# Revit family: Rohrschlaufe SLH
name_source: partatom
category: HLS-Bauteile
revit_build: Autodesk Revit 2017 (Build: 20190507_1515(x64)
units: mm (PartAtom-declared; Revit-internal decimal feet)

## family parameters
Arbeitsebenenbasiert = Ja
Beim Laden mit Abzugskörper schneiden = Nein
Bemaßung runder Anschluss = Durchmesser verwenden
Gemeinsam genutzt = Ja
Immer vertikal = Nein
Raumberechnungspunkt = Nein
Teiletyp = Normal

## types (14) — shared parameters
Fabrikat = Jiangmen Eurofix
Firma = MEFA Befestigungs- und Montagesysteme GmbH
Kurztext1 = Rohrschlaufe SLH
Material = Stahl
Materialname = DX51D
Mengeneinheit = St
Oberflaeche = feuerbandverzinkt
Vorgabe-Ansicht = 1219 mm

## per-type parameters (varying)
| type | Anschluss | Artikelnummer | C | D | EAN | Flanschenmutter | Gewicht | Gewicht pro Bauteil | H | H1 | H2 | Höhe zur Rohrachse | Kurztext2 | MB | MD | Rohraußendurchmesser | Rohraußendurchmesser Zoll | Schlaufentopf | d1 | max. zul. Last | vpe |
| Rohrschlaufe SLH, M10, Ø 33,7 | M10 | 47072034 | 17 mm  [stored 0.0557743 ft] | 34 mm | 4250928450234 | 6kt-Mutter parametrik : Flanschmutter M10 | 0.08 kg | 0.08 kg | 55 mm  [stored 0.180446 ft] | 8 mm  [stored 0.0262467 ft] | 18 mm  [stored 0.0590551 ft] | 63 mm | 1 Zoll / 33,7 mm M10 | 10 mm  [stored 0.0328084 ft] | 2 mm  [stored 0.00656168 ft] | 34 mm | 1 Zoll | Schlaufentopf : Schlaufentopf M10 | 25 mm  [stored 0.082021 ft] | 2.00 kN | 100 St |
| Rohrschlaufe SLH, M10, Ø 42,4 | M10 | 47072042 | 17 mm  [stored 0.0557743 ft] | 42 mm | 4250928450241 | 6kt-Mutter parametrik : Flanschmutter M10 | 0.08 kg | 0.08 kg | 55 mm  [stored 0.180446 ft] | 8 mm  [stored 0.0262467 ft] | 18 mm  [stored 0.0590551 ft] | 68 mm | 1 1/4 Zoll / 42,2 mm M10 | 10 mm  [stored 0.0328084 ft] | 2 mm  [stored 0.00656168 ft] | 42 mm | 1 1/4 Zoll | Schlaufentopf : Schlaufentopf M10 | 25 mm  [stored 0.082021 ft] | 2.00 kN | 100 St |
| Rohrschlaufe SLH, M10, Ø 48,3 | M10 | 47072048 | 17 mm  [stored 0.0557743 ft] | 48 mm | 4250928450258 | 6kt-Mutter parametrik : Flanschmutter M10 | 0.08 kg | 0.08 kg | 60 mm  [stored 0.19685 ft] | 8 mm  [stored 0.0262467 ft] | 18 mm  [stored 0.0590551 ft] | 73 mm | 1 1/2 Zoll / 48,3 mm M10 | 10 mm  [stored 0.0328084 ft] | 2 mm  [stored 0.00656168 ft] | 48 mm | 1 1/2 Zoll | Schlaufentopf : Schlaufentopf M10 | 25 mm  [stored 0.082021 ft] | 2.00 kN | 50 St |
| Rohrschlaufe SLH, M10, Ø 60,3 | M10 | 47072060 | 17 mm  [stored 0.0557743 ft] | 60 mm  [stored 0.19685 ft] | 4250928450265 | 6kt-Mutter parametrik : Flanschmutter M10 | 0.09 kg | 0.09 kg | 69 mm  [stored 0.226378 ft] | 8 mm  [stored 0.0262467 ft] | 18 mm  [stored 0.0590551 ft] | 82 mm | 2 Zoll / 60,3 mm M10 | 10 mm  [stored 0.0328084 ft] | 2 mm  [stored 0.00656168 ft] | 60 mm  [stored 0.19685 ft] | 2 Zoll | Schlaufentopf : Schlaufentopf M10 | 25 mm  [stored 0.082021 ft] | 2.00 kN | 50 St |
| Rohrschlaufe SLH, M10, Ø 76,1 | M10 | 47072076 | 17 mm  [stored 0.0557743 ft] | 76 mm | 4250928450272 | 6kt-Mutter parametrik : Flanschmutter M10 | 0.15 kg | 0.15 kg | 85 mm  [stored 0.278871 ft] | 8 mm  [stored 0.0262467 ft] | 18 mm  [stored 0.0590551 ft] | 99 mm | 2 1/2 Zoll / 76,1 mm M10 | 10 mm  [stored 0.0328084 ft] | 2 mm  [stored 0.00656168 ft] | 76 mm | 2 1/2 Zoll | Schlaufentopf : Schlaufentopf M10 | 25 mm  [stored 0.082021 ft] | 3.50 kN | 50 St |
| Rohrschlaufe SLH, M10, Ø 88,9 | M10 | 47072089 | 17 mm  [stored 0.0557743 ft] | 89 mm | 4250928450289 | 6kt-Mutter parametrik : Flanschmutter M10 | 0.16 kg | 0.16 kg | 100 mm  [stored 0.328084 ft] | 8 mm  [stored 0.0262467 ft] | 18 mm  [stored 0.0590551 ft] | 114 mm | 3 Zoll / 88,9 mm M10 | 10 mm  [stored 0.0328084 ft] | 2 mm  [stored 0.00656168 ft] | 89 mm | 3 Zoll | Schlaufentopf : Schlaufentopf M10 | 25 mm  [stored 0.082021 ft] | 3.50 kN | 25 St |
| Rohrschlaufe SLH, M10, Ø114,3 | M10 | 47072114 | 17 mm  [stored 0.0557743 ft] | 114 mm | 4250928450296 | 6kt-Mutter parametrik : Flanschmutter M10 | 0.19 kg | 0.19 kg | 130 mm  [stored 0.426509 ft] | 8 mm  [stored 0.0262467 ft] | 18 mm  [stored 0.0590551 ft] | 144 mm | 4 Zoll / 114,3 mm M10 | 10 mm  [stored 0.0328084 ft] | 2 mm  [stored 0.00656168 ft] | 114 mm | 4 Zoll | Schlaufentopf : Schlaufentopf M10 | 25 mm  [stored 0.082021 ft] | 3.50 kN | 25 St |
| Rohrschlaufe SLH, M12, Ø139,7 | M12 | 47073140 | 21 mm  [stored 0.0688976 ft] | 140 mm | 4250928450302 | 6kt-Mutter parametrik : Flanschmutter M12 | 0.25 kg | 0.25 kg | 145 mm  [stored 0.475722 ft] | 10 mm  [stored 0.0328084 ft] | 22 mm  [stored 0.0721785 ft] | 161 mm | 5 Zoll / 139,7 mm M12 | 13 mm  [stored 0.0426509 ft] | 3 mm  [stored 0.00984252 ft] | 140 mm | 5 Zoll | Schlaufentopf : Schlaufentopf M12 | 29 mm  [stored 0.0951444 ft] | 5.00 kN | 20 St |
| Rohrschlaufe SLH, M12, Ø168,3 | M12 | 47073168 | 21 mm  [stored 0.0688976 ft] | 168 mm | 4250928450319 | 6kt-Mutter parametrik : Flanschmutter M12 | 0.28 kg | 0.28 kg | 173 mm  [stored 0.567585 ft] | 10 mm  [stored 0.0328084 ft] | 22 mm  [stored 0.0721785 ft] | 189 mm | 6 Zoll / 168,3 mm M12 | 13 mm  [stored 0.0426509 ft] | 3 mm  [stored 0.00984252 ft] | 168 mm | 6 Zoll | Schlaufentopf : Schlaufentopf M12 | 29 mm  [stored 0.0951444 ft] | 5.00 kN | 20 St |
| Rohrschlaufe SLH, M16, Ø219,1 | M16 | 47073219 | 27 mm  [stored 0.0885827 ft] | 219 mm  [stored 0.718504 ft] | 4250928450326 | 6kt-Mutter parametrik : Flanschmutter M16 | 0.61 kg | 0.61 kg | 220 mm  [stored 0.721785 ft] | 14 mm  [stored 0.0459318 ft] | 29 mm  [stored 0.0951444 ft] | 241 mm | 8 Zoll / 219 mm M16 | 13 mm  [stored 0.0426509 ft] | 3 mm  [stored 0.00984252 ft] | 219 mm  [stored 0.718504 ft] | 8 Zoll | Schlaufentopf : Schlaufentopf M16 | 37 mm  [stored 0.121391 ft] | 8.50 kN | 10 St |
| Rohrschlaufe SLH, M 8, Ø 33,7 | M8 | 47072033 | 15 mm  [stored 0.0492126 ft] | 34 mm | 4250928455741 | 6kt-Mutter parametrik : Flanschmutter M8 (0470008) | 0.06 kg | 0.06 kg | 61 mm  [stored 0.200131 ft] | 7 mm  [stored 0.0229659 ft] | 15 mm  [stored 0.0492126 ft] | 61 mm | 1 Zoll / 33,7 mm M8 | 10 mm  [stored 0.0328084 ft] | 2 mm  [stored 0.00656168 ft] | 34 mm | 1 Zoll | Schlaufentopf : Schlaufentopf M8 | 22 mm  [stored 0.0721785 ft] | 2.00 kN | 100 St |
| Rohrschlaufe SLH, M 8, Ø 42,4 | M8 | 47072041 | 15 mm  [stored 0.0492126 ft] | 42 mm | 4250928455758 | 6kt-Mutter parametrik : Flanschmutter M8 (0470008) | 0.07 kg | 0.07 kg | 66 mm  [stored 0.216535 ft] | 7 mm  [stored 0.0229659 ft] | 15 mm  [stored 0.0492126 ft] | 66 mm | 1 1/4 Zoll / 42,4 mm M8 | 10 mm  [stored 0.0328084 ft] | 2 mm  [stored 0.00656168 ft] | 42 mm | 1 1/4 Zoll | Schlaufentopf : Schlaufentopf M8 | 22 mm  [stored 0.0721785 ft] | 2.00 kN | 100 St |
| Rohrschlaufe SLH, M 8, Ø 48,3 | M8 | 47072047 | 15 mm  [stored 0.0492126 ft] | 48 mm | 4250928455765 | 6kt-Mutter parametrik : Flanschmutter M8 (0470008) | 0.07 kg | 0.07 kg | 71 mm  [stored 0.23294 ft] | 7 mm  [stored 0.0229659 ft] | 15 mm  [stored 0.0492126 ft] | 71 mm | 1 1/2 Zoll / 48,3 mm M8 | 10 mm  [stored 0.0328084 ft] | 2 mm  [stored 0.00656168 ft] | 48 mm | 1 1/2 Zoll | Schlaufentopf : Schlaufentopf M8 | 22 mm  [stored 0.0721785 ft] | 2.00 kN | 100 St |
| Rohrschlaufe SLH, M 8, Ø 60,3 | M8 | 47072059 | 15 mm  [stored 0.0492126 ft] | 60 mm  [stored 0.19685 ft] | 4250928455772 | 6kt-Mutter parametrik : Flanschmutter M8 (0470008) | 0.07 kg | 0.07 kg | 80 mm  [stored 0.262467 ft] | 7 mm  [stored 0.0229659 ft] | 15 mm  [stored 0.0492126 ft] | 80 mm | 2 Zoll / 60,3 mm M8 | 10 mm  [stored 0.0328084 ft] | 2 mm  [stored 0.00656168 ft] | 60 mm  [stored 0.19685 ft] | 2 Zoll | Schlaufentopf : Schlaufentopf M8 | 22 mm  [stored 0.0721785 ft] | 2.00 kN | 100 St |

note: [stored X ft] marks values corroborated as IEEE doubles in the binary element streams (Revit-internal decimal feet)

## geometry (parser evidence)
native form markers: Sweep x3
no freeform markers — native parametric forms only
